FCSTD DOCUMENT  (FreeCAD 0.21R33771 (Git))
Label: Stator_Coils
License: All rights reserved
LicenseURL: http://en.wikipedia.org/wiki/All_rights_reserved
objects: App::Link×1, Part::FeaturePython×1, Spreadsheet::Sheet×1
EXTERNAL_REF file=Stator_Coil_Triangular.FCStd obj=Body
EXTERNAL_REF file=../../Master_of_Puppets.FCStd obj=Alternator
EXTERNAL_REF file=../../Master_of_Puppets.FCStd obj=Spreadsheet
EXTERNAL_REF file=Stator_Coil.FCStd obj=Body001
EXTERNAL_REF file=Stator_Coil_Triangular_Reduced.FCStd obj=Body

FEATURE [App::Link] Link  label="Coil"
  LinkPlacement = pos=(0,99.3115,0) rot=(0,0,1;0rad)
  LinkTransform = true
  LinkedObject = -> <external Stator_Coil_Triangular.FCStd>#Body
  Placement = pos=(0,99.3115,0) rot=(0,0,1;0rad)
  expr: .LinkPlacement.Base.y = Spreadsheet.CoilY
  expr: LinkedObject = Spreadsheet.Coil
FEATURE [Part::FeaturePython] Array  label="Stator_Coils"  # Draft array (typed FeaturePython)
  AlwaysSyncPlacement = false
  Angle = 360
  ArrayType = 1
  Axis = (0,0,1)
  Base = -> Link
  Center = (0,0,0)
  Count = 9
  ExpandArray = false
  Fuse = false
  IntervalAxis = (0,0,0)
  IntervalX = (50,0,0)
  IntervalY = (0,50,0)
  IntervalZ = (0,0,50)
  NumberCircles = 1
  NumberPolar = 9
  NumberX = 2
  NumberY = 2
  NumberZ = 1
  Placement = pos=(0,0,0.1) rot=(0,0,1;0rad)
  PlacementList = 9 placements: [(0,99.3115,0),(-63.8362,76.077,0),(-97.8028,17.2453,0),(-86.0063,-49.6558,0),(-33.9665,-93.3223,0),(33.9665,-93.3223,0),(86.0063,-49.6558,0),(97.8028,17.2453,0),(63.8362,76.077,0)]
  RadialDistance = 50
  ScaleList = (9) [(1,1,1),(1,1,1),(1,1,1),(1,1,1),(1,1,1),(1,1,1),(1,1,1),(1,1,1),(1,1,1)]
  Symmetry = 1
  TangentialDistance = 25
  expr: .Placement.Base.z = Spreadsheet.ThicknessOffset / 2
  expr: NumberPolar = Spreadsheet.NumberOfCoils
FEATURE [Spreadsheet::Sheet] Spreadsheet
  cells = A1='Inputs; A2='CoilType; B2(CoilType)==Master_of_Puppets#Spreadsheet.CoilType; A3='NumberOfCoils; B3(NumberOfCoils)==Master_of_Puppets#Alternator.NumberOfCoils; A4='StatorInnerHoleRadius; B4(StatorInnerHoleRadius)==Master_of_Puppets#Alternator.StatorInnerHoleRadius; A5='DoCoilsOverlap; B5(DoCoilsOverlap)==Master_of_Puppets#Alternator.DoCoilsOverlap; A6='CoilLegWidth; B6(CoilLegWidth)==Master_of_Puppets#Spreadsheet.CoilLegWidth; A7='Coil; A8='CoilY; B8(CoilY)==StatorInnerHoleRadius + (CoilType == 3 ? CoilLegWidth : 0); C8='TODO: If we position bottom-most part of triangular coil to be aligned with x-axis in their documents. then we can remove adding the CoilLegWidth logic here.; A9='Coil; B9(Coil)==CoilType != 3 ? <<Stator_Coil>>#<<Stator_Coil>>._self : (DoCoilsOverlap == 0 ? <<Stator_Coil_Triangular>>#<<Stator_Coil>>._self : <<Stator_Coil_Triangular_Reduced>>#<<Stator_Coil>>._self); A10='Static; A11='ThicknessOffset; B11(ThicknessOffset)=0.2; C11='Duplicated in Coil
